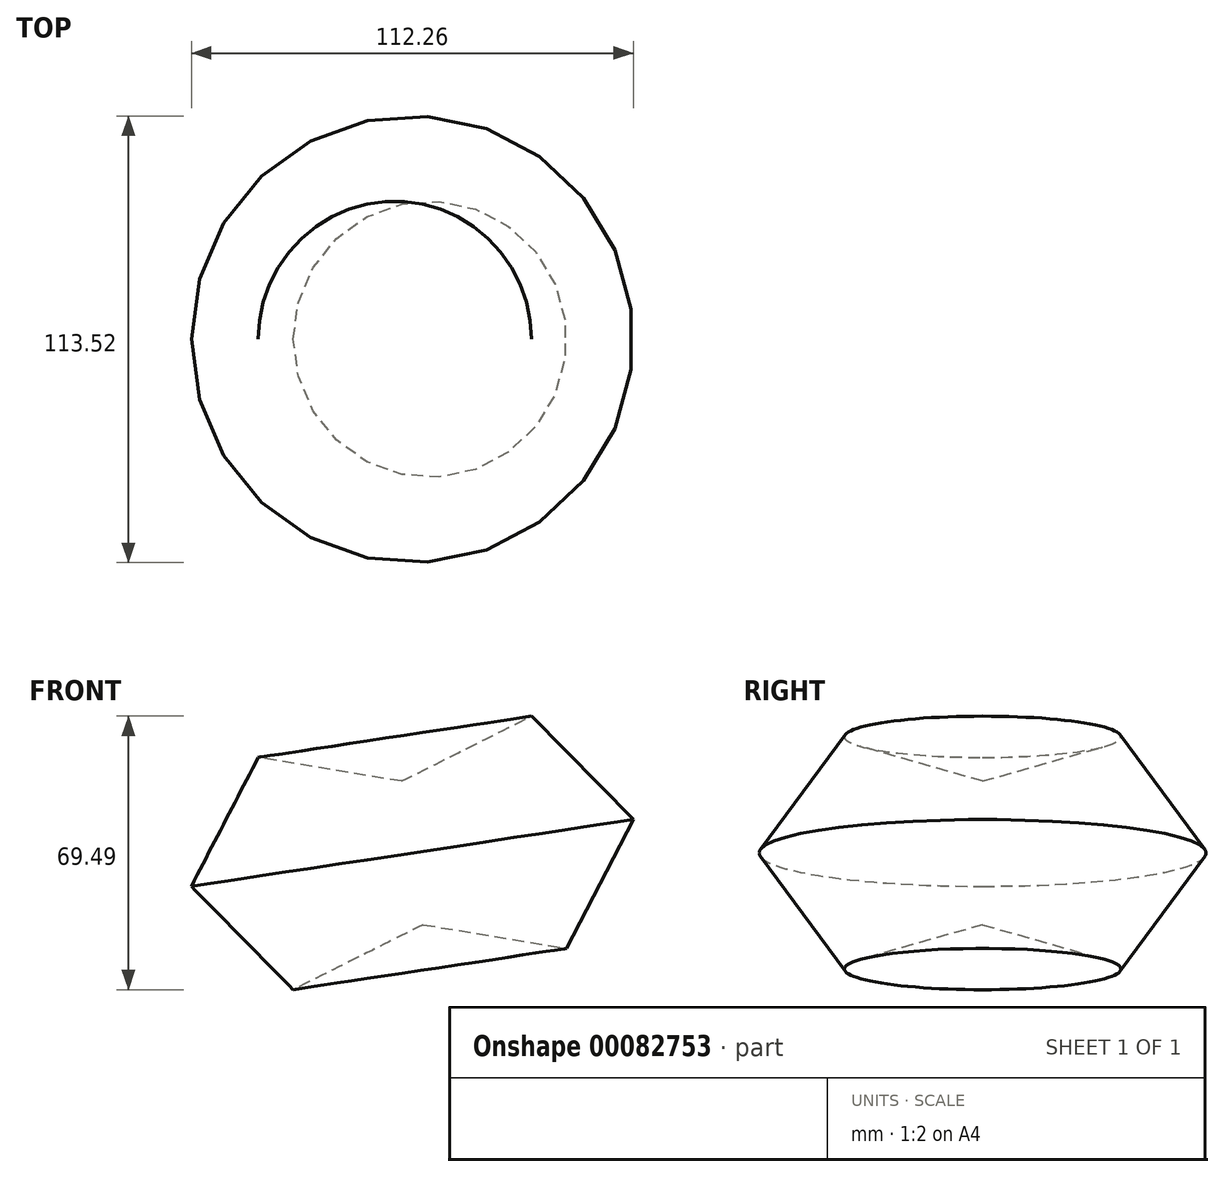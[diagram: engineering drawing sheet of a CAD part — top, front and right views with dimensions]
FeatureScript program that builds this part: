
annotation { "Feature Type Name" : "Feature", "Feature Type Description" : "" }
export const myFeature = defineFeature(function(context is Context, id is Id, definition is map)
    precondition{}
    {
        {
            var Q0;
            Q0=qCreatedBy(makeId("Front.planeOp"),FACE);
            var sketch = newSketch(context, id + "F0", { "sketchPlane" : qUnion([Q0])});
            skCircle(sketch, "E0.cCircle", {"center": v(0, 0) * mm, "radius": 25.39 * mm, "construction": true});
            skLineSegment(sketch, "E0.0", {"start": v(5.13, 30.96) * mm, "end": v(31.03, 4.68) * mm});
            skLineSegment(sketch, "E0.1", {"start": v(31.03, 4.68) * mm, "end": v(14.04, -28.06) * mm});
            skLineSegment(sketch, "E0.2", {"start": v(14.04, -28.06) * mm, "end": v(-22.35, -22.03) * mm});
            skLineSegment(sketch, "E0.3", {"start": v(-22.35, -22.03) * mm, "end": v(-27.85, 14.45) * mm});
            skLineSegment(sketch, "E0.4", {"start": v(-27.85, 14.45) * mm, "end": v(5.13, 30.96) * mm});
            skPoint(sketch, "E0.0.midPoint", {"position": v(18.08, 17.82) * mm});
            skSolve(sketch);
        }
        {
            var Q0;
            Q0 = qSketchRegion(id + "F0", true);
            var Q1;
            Q1=sQuery(id+"F0.wireOp",EDGE,"E0.3");
            revolve(context, id + "F1", {"entities" : qUnion([Q0]), "axis" : qUnion([Q1]), "revolveType" : RevolveType.FULL});
        }
    });
